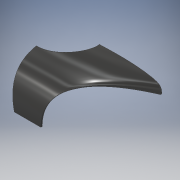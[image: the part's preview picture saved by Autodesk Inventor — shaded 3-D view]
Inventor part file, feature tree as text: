
AUTODESK INVENTOR PART (.ipt)
format: ipt  version: 2019 (Build 230136000, 136)  size: 1,314,304 bytes
history: native  units: mm
features: plane x27, sketch x24, extrude x11, fillet x6, mirror x5, loft x4, chamfer x3, other x1
ambient origin geometry x8: Origin, YZ Plane, XZ Plane, XY Plane, X Axis, Y Axis, Z Axis, Center Point
bodies: Body1 (feature_tree)
feature tree (81):
  sketch  "Sketch1"  dims[d2=55.0mm d5=-107.0mm d13=5.0mm d14=50.0mm]
  plane  "Work Plane1"
  sketch  "Sketch2"  dims[d15=70.0mm d16=5.0mm]
  sketch  "Sketch3"  dims[d17=0.0mm d18=90.0deg d19=0.0mm d20=90.0deg d21=0.0mm d22=90.0deg d23=2.0mm]
  plane  "Work Plane2"
  loft  "Loft2"
  mirror  "Mirror2"
  fillet  "Fillet1"  Radius=5.0mm
  fillet  "Fillet4"  Radius=50.0mm
  plane  "Work Plane3"
  plane  "Work Plane4"
  extrude  "Extrusion1"  Depth=5.0mm
  plane  "Work Plane5"
  extrude  "Extrusion2"  TaperAngle=0.0deg  [1 undecoded]
  fillet  "Fillet5"  [1 undecoded]
  mirror  "Mirror3"
  plane  "Work Plane22"
  plane  "Work Plane6"
  plane  "Work Plane7"
  fillet  "Fillet11"  Radius=2.0mm
  extrude  "Extrusion7"  Depth=87.5mm
  mirror  "Mirror4"
  plane  "Work Plane8"
  plane  "Work Plane9"
  sketch  "Sketch20"  dims[d42=2.0mm]
  plane  "Work Plane10"
  sketch  "Sketch21"  dims[d43=2.0mm]
  plane  "Work Plane11"
  sketch  "Sketch22"  dims[d44=2.0mm]
  loft  "Loft5"
  plane  "Work Plane13"
  sketch  "Sketch25"  dims[d45=2.0mm]
  plane  "Work Plane18"
  loft  "Loft6"
  mirror  "Mirror5"
  plane  "Work Plane19"
  extrude  "Extrusion9"  Depth=2.0mm
  fillet  "Fillet12"  Radius=2.0mm
  fillet  "Fillet14"  Radius=2.0mm
  plane  "Work Plane20"
  plane  "Work Plane21"
  plane  "Work Plane23"
  plane  "Work Plane24"
  plane  "Work Plane25"
  sketch  "Sketch33"  dims[d48=2.0mm]
  plane  "Work Plane26"
  sketch  "Sketch34"  dims[d49=2.0mm d50=2.0mm d51=1.0mm]
  plane  "Work Plane27"
  sketch  "Sketch35"  dims[d79=-25.0mm]
  plane  "Work Plane30"
  sketch  "Sketch38"  dims[d84=2.0mm]
  plane  "Work Plane31"
  plane  "Work Plane35"
  chamfer  "Chamfer7"  Distance=2.0mm
  chamfer  "Chamfer8"  Distance=28.0mm
  chamfer  "Chamfer9"  Distance=22.0mm
  loft  "Loft10"
  mirror  "Mirror9"
  plane  "Work Plane37"
  extrude  "Extrusion24"  Depth=70.0mm
  extrude  "Extrusion25"  Depth=10.0mm
  extrude  "Extrusion26"  Depth=10.0mm
  extrude  "Extrusion27"  TaperAngle=0.0deg  [1 undecoded]
  plane  "Work Plane38"
  extrude  "Extrusion28"  TaperAngle=0.0deg  [1 undecoded]
  extrude  "Extrusion29"  TaperAngle=0.0deg  [1 undecoded]
  extrude  "Extrusion30"  [1 undecoded]
  sketch  "Sketch4"  dims[d29=1.0mm d30=-4.5mm d31=87.5mm]
  sketch  "Sketch5"  dims[d32=0.0mm d33=0.0mm d34=-28.0mm]
  sketch  "Sketch6"  dims[d35=15.0mm d36=3.0mm]
  sketch  "Sketch17"  dims[d37=0.0mm d38=0.0mm d39=2.0mm d40=2.0mm d41=2.0mm]
  sketch  "Sketch27"  dims[d46=2.0mm]
  other  "Edges1"
  sketch  "Sketch28"  dims[d47=2.0mm]
  sketch  "Sketch47"  dims[d85=13.5mm]
  sketch  "Sketch48"  dims[d86=2.5mm]
  sketch  "Sketch49"  dims[d87=5.0mm]
  sketch  "Sketch50"  dims[d88=6.25mm d89=28.0mm d90=0.0mm d91=22.0mm d101=200.0mm]
  sketch  "Sketch51"  dims[d104=5.0mm d105=50.0mm d106=-80.0mm d107=45.0mm]
  sketch  "Sketch52"  dims[d108=3.0mm d109=70.0mm]
  sketch  "Sketch53"  dims[d110=80.0mm d111=3.0mm d112=20.0mm d123=0.0mm d124=90.0deg d125=0.0mm d126=90.0deg d127=0.0mm d128=90.0deg d129=-20.0mm d131=2.0mm d132=80.0mm d133=10.0mm d134=0.0mm d135=0.0mm d136=90.0deg d137=0.0mm d138=90.0deg d139=0.0mm d140=90.0deg d141=3.0mm d142=7.0mm d143=10.0mm d144=0.0mm d145=70.0mm d147=10.0mm d171=35.75mm d174=-8.25mm d177=20.0mm d179=30.0mm d180=5.0mm d181=41.5mm d182=15.0mm d183=10.0mm d184=5.0mm d200=-2.0mm d219=15.0mm d241=2.0mm d242=2.0mm d243=45.0deg d244=1.0mm d245=2.0mm d246=45.0deg d247=0.5mm d248=2.0mm d249=45.0deg d250=5.0mm d251=0.0mm d252=90.0deg d253=0.0mm d254=90.0deg d255=0.0mm d256=90.0deg d261=0.0mm d262=0.0mm d263=10.0mm d264=0.0mm d265=5.0mm d266=0.0mm d267=4.0mm d268=20.0mm d269=0.0mm d270=16.0mm d271=14.0mm d272=20.0mm d273=0.0mm d274=4.0mm d275=20.0mm d276=0.0mm d277=0.0mm d278=0.0mm]
note: 6 required parameter values undecoded (feature->parameter linkage not recoverable at this tier; creation-order binding heuristic only, values carry confidence <= 0.55)
